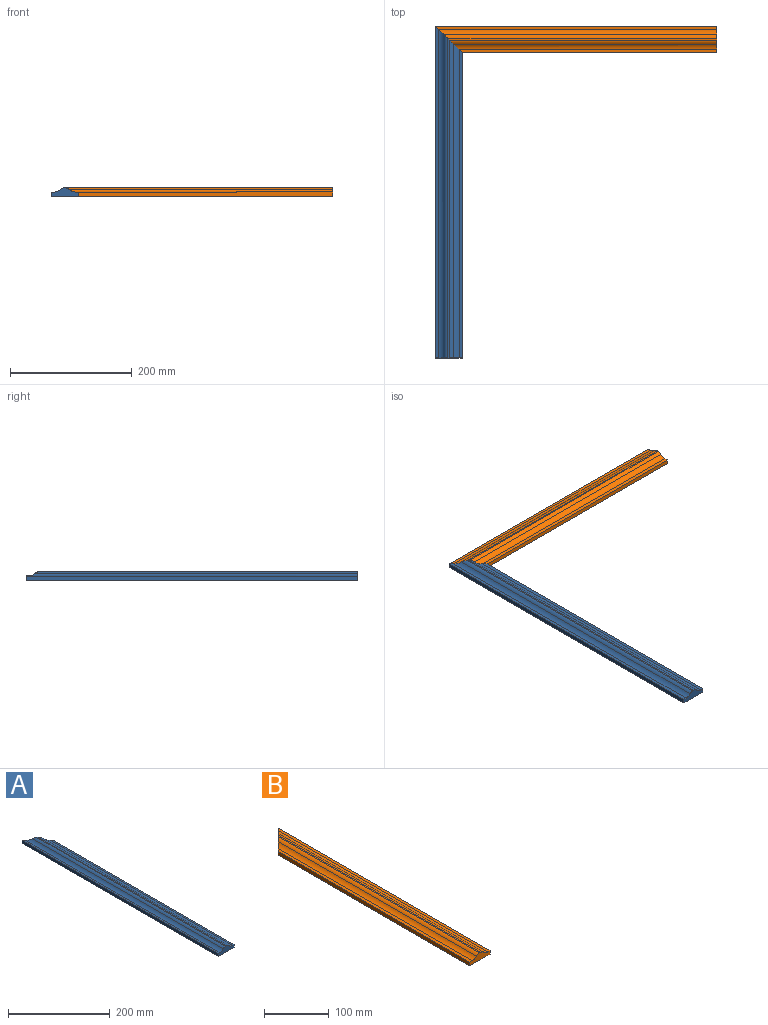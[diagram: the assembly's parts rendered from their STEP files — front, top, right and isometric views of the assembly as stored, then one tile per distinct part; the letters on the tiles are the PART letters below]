
ASSEMBLY  parts=2 mates=1
PART A: 12 faces, bbox 44x545x14 mm
  f0: cylinder r=9.73mm len=530.66mm, axis (0,1,0), area 3832.6mm2, adj f1,f9,f10,f11
  f1: cylinder r=12.89mm len=540mm, axis (0,1,0), area 5585.8mm2, adj f0,f2,f10,f11
  f2: plane 545x5mm, normal (0,0,1), area 2712.5mm2, adj f1,f3,f10,f11
  f3: plane 545x7mm, normal (-1,0,0), area 3815mm2, adj f2,f4,f10,f11
  f4: plane 545x44mm, normal (0,0,-1), area 23012mm2, adj f3,f5,f10,f11
  f5: plane 501x7mm, normal (1,0,0), area 3507mm2, adj f4,f6,f10,f11
  f6: plane 506x5mm, normal (0,0,1), area 2517.5mm2, adj f5,f7,f10,f11
  f7: cylinder r=12.89mm len=515.34mm, axis (0,1,0), area 5334mm2, adj f6,f8,f10,f11
  f8: cylinder r=9.73mm len=521.77mm, axis (0,1,0), area 3765.3mm2, adj f7,f9,f10,f11
  f9: plane 524.23x2.47mm, normal (0,0,1), area 1289.7mm2, adj f0,f8,f10,f11
  f10: plane 44x14mm, normal (0,-1,0), area 425.5mm2, adj f0,f1,f2,f3,f4,f5,f6,f7
  f11: plane 44x44mm, normal (0.71,0.71,0), area 601.7mm2, adj f0,f1,f2,f3,f4,f5,f6,f7
PART B: 12 faces, bbox 44x462x14 mm
  f0: cylinder r=9.73mm len=438.77mm, axis (0,1,0), area 3162.4mm2, adj f1,f9,f10,f11
  f1: cylinder r=12.89mm len=432.34mm, axis (0,1,0), area 4467.5mm2, adj f0,f2,f10,f11
  f2: plane 423x5mm, normal (0,0,1), area 2102.5mm2, adj f1,f3,f10,f11
  f3: plane 418x7mm, normal (-1,0,0), area 2926mm2, adj f2,f4,f10,f11
  f4: plane 462x44mm, normal (0,0,-1), area 19360mm2, adj f3,f5,f10,f11
  f5: plane 462x7mm, normal (1,0,0), area 3234mm2, adj f4,f6,f10,f11
  f6: plane 462x5mm, normal (0,0,1), area 2297.5mm2, adj f5,f7,f10,f11
  f7: cylinder r=12.89mm len=457mm, axis (0,1,0), area 4719.3mm2, adj f6,f8,f10,f11
  f8: cylinder r=9.73mm len=447.66mm, axis (0,1,0), area 3229.7mm2, adj f7,f9,f10,f11
  f9: plane 441.23x2.47mm, normal (0,0,1), area 1085mm2, adj f0,f8,f10,f11
  f10: plane 44x14mm, normal (0,-1,0), area 425.5mm2, adj f0,f1,f2,f3,f4,f5,f6,f7
  f11: plane 44x44mm, normal (-0.71,0.71,0), area 601.7mm2, adj f0,f1,f2,f3,f4,f5,f6,f7
PLACE A at identity
PLACE B rot(axis=(0,0,1),90deg) t=(209,250.5,0)mm
MATE fastened B.f11 <-> A.f11  axis (-0.71,-0.71,0) through (0,250.5,-1.77)mm
